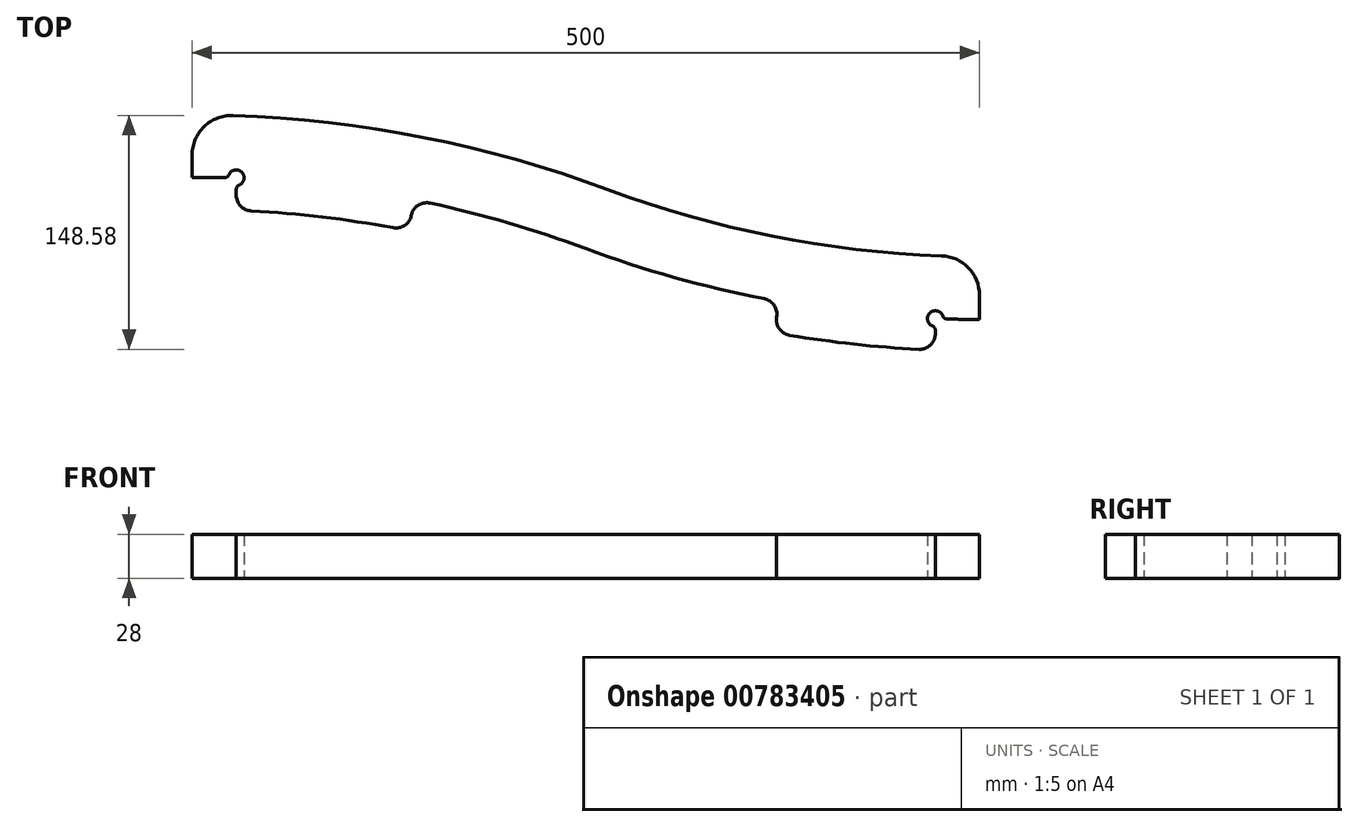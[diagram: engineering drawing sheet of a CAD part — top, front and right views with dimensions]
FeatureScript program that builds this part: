
annotation { "Feature Type Name" : "Feature", "Feature Type Description" : "" }
export const myFeature = defineFeature(function(context is Context, id is Id, definition is map)
    precondition{}
    {
        {
            var Q0;
            Q0=qCreatedBy(makeId("Top.planeOp"),FACE);
            var sketch = newSketch(context, id + "F0", { "sketchPlane" : qUnion([Q0])});
            skLineSegment(sketch, "E0", {"start": v(0, 140) * mm, "end": v(0, -140) * mm});
            skLineSegment(sketch, "E1", {"start": v(500, 50) * mm, "end": v(500, -50) * mm});
            skArc(sketch, "E2", {"start": v(250, 95) * mm, "mid": v(201.06, 111.23) * mm, "end": v(151.09, 123.9) * mm});
            skArc(sketch, "E3", {"start": v(250, 95) * mm, "mid": v(306, 76.75) * mm, "end": v(363.3, 63.15) * mm});
            skArc(sketch, "E4.0", {"start": v(263.95, 132.49) * mm, "mid": v(146.8, 165.63) * mm, "end": v(25.85, 179.56) * mm});
            skArc(sketch, "E5.0", {"start": v(263.95, 132.49) * mm, "mid": v(368.23, 102.95) * mm, "end": v(475.9, 90.43) * mm});
            skLineSegment(sketch, "E6", {"start": v(0, 140) * mm, "end": v(0, 154.57) * mm});
            skLineSegment(sketch, "E7", {"start": v(500, 50) * mm, "end": v(500, 65.45) * mm});
            skLineSegment(sketch, "E8", {"start": v(-157.4, 0) * mm, "end": v(716.34, 0) * mm, "construction": true});
            skPoint(sketch, "E9.visualSharp", {"position": v(0, 180) * mm});
            skArc(sketch, "E9.filletArc", {"start": v(25.85, 179.56) * mm, "mid": v(7.63, 172.55) * mm, "end": v(0, 154.57) * mm});
            skPoint(sketch, "E10.visualSharp", {"position": v(500, 90) * mm});
            skArc(sketch, "E10.filletArc", {"start": v(500, 65.45) * mm, "mid": v(492.99, 82.8) * mm, "end": v(475.9, 90.43) * mm});
            skArc(sketch, "E11.0", {"start": v(127.54, 108.23) * mm, "mid": v(82.68, 115.08) * mm, "end": v(37.46, 119) * mm});
            skLineSegment(sketch, "E12.0", {"start": v(28, 132.58) * mm, "end": v(28, 128.98) * mm});
            skArc(sketch, "E13.0", {"start": v(379.44, 39.93) * mm, "mid": v(420.33, 34.32) * mm, "end": v(461.48, 31) * mm});
            skLineSegment(sketch, "E14", {"start": v(139.18, 116.1) * mm, "end": v(139.18, 116.1) * mm});
            skPoint(sketch, "E15.orphan", {"position": v(137.22, 106.36) * mm});
            skLineSegment(sketch, "E16", {"start": v(371.23, 51.57) * mm, "end": v(371.23, 51.57) * mm});
            skPoint(sketch, "E17.orphan", {"position": v(373, 61.34) * mm});
            skLineSegment(sketch, "E18", {"start": v(472, 41) * mm, "end": v(472, 43.13) * mm});
            skArc(sketch, "E19.trimOffspring", {"start": v(479.43, 50.3) * mm, "mid": v(489.71, 50.07) * mm, "end": v(500, 50) * mm});
            skPoint(sketch, "E20.visualSharp", {"position": v(28, 119.44) * mm});
            skArc(sketch, "E20.filletArc", {"start": v(28, 128.98) * mm, "mid": v(30.74, 122.1) * mm, "end": v(37.46, 119) * mm});
            skArc(sketch, "E21.filletArc", {"start": v(127.54, 108.23) * mm, "mid": v(134.97, 109.78) * mm, "end": v(139.18, 116.1) * mm});
            skPoint(sketch, "E22.visualSharp", {"position": v(141.16, 125.97) * mm});
            skArc(sketch, "E22.filletArc", {"start": v(151.09, 123.9) * mm, "mid": v(143.5, 122.49) * mm, "end": v(139.18, 116.1) * mm});
            skArc(sketch, "E23.filletArc", {"start": v(371.23, 51.57) * mm, "mid": v(369.64, 58.99) * mm, "end": v(363.3, 63.15) * mm});
            skPoint(sketch, "E24.visualSharp", {"position": v(369.45, 41.66) * mm});
            skArc(sketch, "E24.filletArc", {"start": v(371.23, 51.57) * mm, "mid": v(372.9, 44.03) * mm, "end": v(379.44, 39.93) * mm});
            skPoint(sketch, "E25.visualSharp", {"position": v(472, 30.53) * mm});
            skArc(sketch, "E25.filletArc", {"start": v(461.48, 31) * mm, "mid": v(468.88, 33.74) * mm, "end": v(472, 41) * mm});
            skArc(sketch, "E26", {"start": v(29.88, 135.36) * mm, "mid": v(31.54, 143.54) * mm, "end": v(23.36, 141.88) * mm});
            skArc(sketch, "E27", {"start": v(476.7, 52.26) * mm, "mid": v(468.52, 54.14) * mm, "end": v(470.12, 45.91) * mm});
            skPoint(sketch, "E28.visualSharp", {"position": v(472, 45.55) * mm});
            skArc(sketch, "E28.filletArc", {"start": v(472, 43.13) * mm, "mid": v(471.49, 44.8) * mm, "end": v(470.12, 45.91) * mm});
            skPoint(sketch, "E29.visualSharp", {"position": v(477, 50.37) * mm});
            skArc(sketch, "E29.filletArc", {"start": v(476.7, 52.26) * mm, "mid": v(477.76, 50.86) * mm, "end": v(479.43, 50.3) * mm});
            skPoint(sketch, "E30.visualSharp", {"position": v(28, 135) * mm});
            skArc(sketch, "E30.filletArc", {"start": v(29.88, 135.36) * mm, "mid": v(28.51, 134.26) * mm, "end": v(28, 132.58) * mm});
            skLineSegment(sketch, "E31", {"start": v(0, 140) * mm, "end": v(20.58, 140) * mm});
            skPoint(sketch, "E32.visualSharp", {"position": v(23, 140) * mm});
            skArc(sketch, "E32.filletArc", {"start": v(20.58, 140) * mm, "mid": v(22.26, 140.51) * mm, "end": v(23.36, 141.88) * mm});
            skSolve(sketch);
        }
        {
            var Q0;
            Q0=makeQuery(id+"F0.imprint","IMPRINT",FACE,{"disambiguationData":[TD([[makeQuery(id+"F0.imprint","IMPRINT",EDGE,{"derivedFrom":sQuery(id+"F0.wireOp",EDGE,"E2")}),-1.0]])]});
            extrude(context, id + "F1", {"entities" : qUnion([Q0]), "depth" : 28 * mm, "offsetDistance" : 25 * mm});
        }
    });
